# Revit family: Toilet-Floor_Mount-KOHLER-Irvine-K-90097_1
name_source: partatom
category: Plumbing Fixtures
units: mm (PartAtom-declared; Revit-internal decimal feet)

## family parameters
Cut with Voids When Loaded = No
Host = Face
OmniClass Number = 23.31.19.00
OmniClass Title = Toilets
Part Type = Normal
Room Calculation Point = No
Round Connector Dimension = Use Diameter
Shared = No

## types (5) — shared parameters
ADA Compliant = Yes
Assembly Code = D2010100
Bowl Height = 16 3/8"
CW Connection = Yes
Cold Water Inlet = Cold Water Inlet
Date Modified = 05/19/2023
Default Elevation = 0"
Description = ContinuousClean Two-Piece Elongated Toilet With Skirted Trapway, 1.28 gpf
Flow Rate = 0 GPM
Flush Rate- GPF = 1.28 GPF
Flush Rate- LPF = 4.8 LPF
HW Connection = No
Height = 31 1/2"
Hot Water Inlet = Hot Water Inlet
Length = 29 5/16"
Manufacturer = Kohler Co.
Master Format 2014 = 22 42 13.13
Master Format 2014 Name = Residential Water Closets
Material = Vitreous China
Pressure = 80.00 psi
Product Documentation Link = https://www.us.kohler.com
Product Name = Irvine
Product Page URL = http://www.us.kohler.com
Rough-In = 12"
Seat Included = No
URL = https://www.us.kohler.com
Vent Connection = No
Waste Connection = Yes
Waste Water Outlet = Waste Water Outlet
WaterSense Certified = Yes
Width = 14 7/16"

## per-type parameters (varying)
| type | Finish | Model | Type |
| 0-White | Kohler-Vitreous_China-0-White | K-90097-0 | 1 |
| 7-Black Black | Kohler-Vitreous_China-7-Black_Black | K-90097-7 | 2 |
| 95-Ice Grey | Kohler-Vitreous_China-95-Ice_Grey | K-90097-95 | 3 |
| 96-Biscuit | Kohler-Vitreous_China-96-Biscuit | K-90097-96 | 4 |
| NY-Dune | Kohler-Vitreous_China-NY-Dune | K-90097-NY | 5 |

## geometry (parser evidence)
native form markers: Sweep x5
no freeform markers — native parametric forms only
